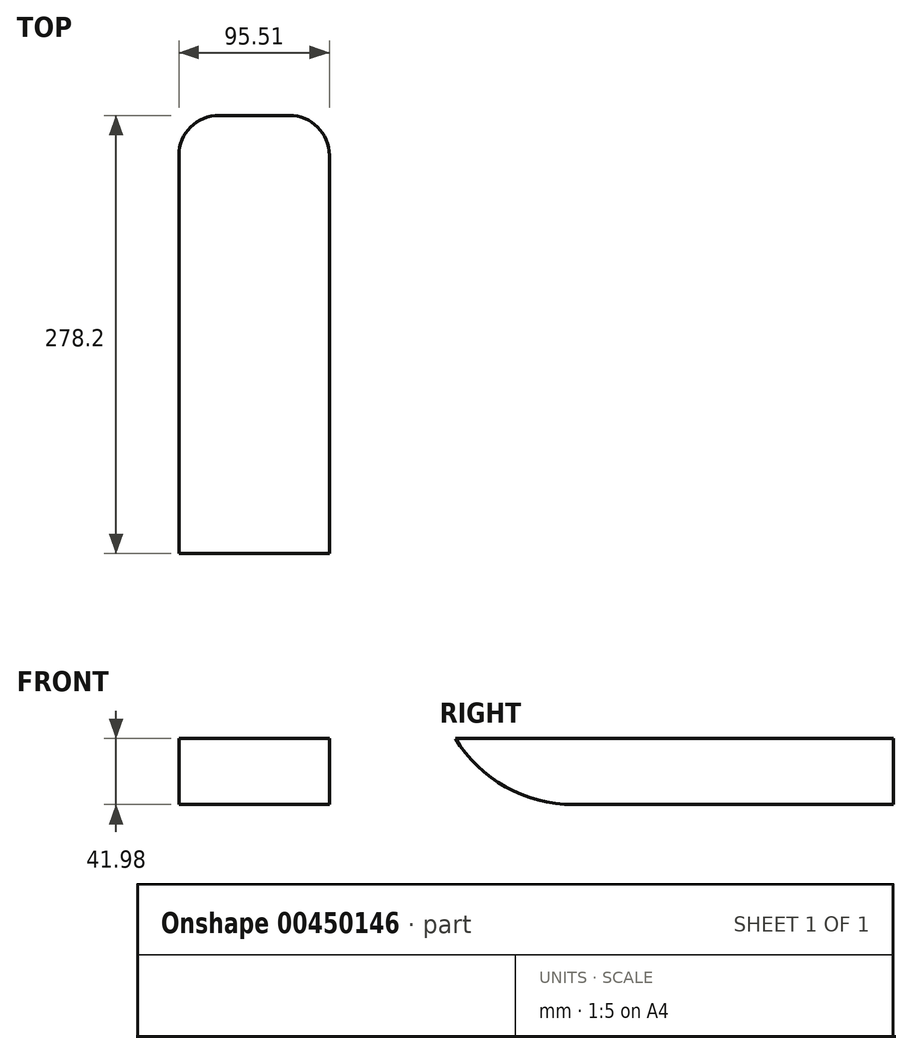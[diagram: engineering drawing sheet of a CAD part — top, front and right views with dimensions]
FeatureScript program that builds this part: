
annotation { "Feature Type Name" : "Feature", "Feature Type Description" : "" }
export const myFeature = defineFeature(function(context is Context, id is Id, definition is map)
    precondition{}
    {
        {
            var Q0;
            Q0=qCreatedBy(makeId("Front.planeOp"),FACE);
            var sketch = newSketch(context, id + "F0", { "sketchPlane" : qUnion([Q0])});
            skLineSegment(sketch, "E0.bottom", {"start": v(-38.5, 14.2) * mm, "end": v(57, 14.2) * mm});
            skLineSegment(sketch, "E0.top", {"start": v(-38.5, -27.77) * mm, "end": v(57, -27.77) * mm});
            skLineSegment(sketch, "E0.left", {"start": v(-38.5, 14.2) * mm, "end": v(-38.5, -27.77) * mm});
            skLineSegment(sketch, "E0.right", {"start": v(57, 14.2) * mm, "end": v(57, -27.77) * mm});
            skSolve(sketch);
        }
        {
            var Q0;
            Q0 = qSketchRegion(id + "F0", true);
            extrude(context, id + "F1", {"entities" : qUnion([Q0]), "depth" : 101.6 * mm, "hasSecondDirection" : true, "secondDirectionOppositeDirection" : true, "secondDirectionDepth" : 101.6 * mm});
        }
        {
            var Q0;
            Q0=makeQuery(id+"F1.opExtrude","CAP_EDGE",EDGE,{"disambiguationData":[OSD([sQuery(id+"F0.wireOp",EDGE,"E0.right")])],"isStart":true});
            var Q1;
            Q1=makeQuery(id+"F1.opExtrude","CAP_EDGE",EDGE,{"disambiguationData":[OSD([sQuery(id+"F0.wireOp",EDGE,"E0.left")])],"isStart":true});
            fillet(context, id + "F2", {"entities" : qUnion([Q0, Q1]), "radius" : 25.4 * mm, "tangentPropagation" : true, "allowEdgeOverflow" : false});
        }
        {
            var Q0;
            Q0=makeQuery(id+"F1.opExtrude","SWEPT_FACE",FACE,{"disambiguationData":[OSD([sQuery(id+"F0.wireOp",EDGE,"E0.right")])]});
            var sketch = newSketch(context, id + "F3", { "sketchPlane" : qUnion([Q0])});
            skLineSegment(sketch, "E1", {"start": v(-101.6, 14.2) * mm, "end": v(-176.6, 14.2) * mm});
            skArc(sketch, "E2", {"start": v(-176.6, 14.2) * mm, "mid": v(-144.57, -16.56) * mm, "end": v(-101.6, -27.77) * mm});
            skSolve(sketch);
        }
        {
            var Q0;
            Q0=makeQuery(id+"F3.imprint","IMPRINT",FACE,{"disambiguationData":[TD([[makeQuery(id+"F3.imprint","IMPRINT",EDGE,{"derivedFrom":sQuery(id+"F3.wireOp",EDGE,"E1")}),1.0]])]});
            extrude(context, id + "F4", {"entities" : qUnion([Q0]), "operationType" : NewBodyOperationType.ADD, "oppositeDirection" : true, "depth" : 95.5 * mm});
        }
    });
